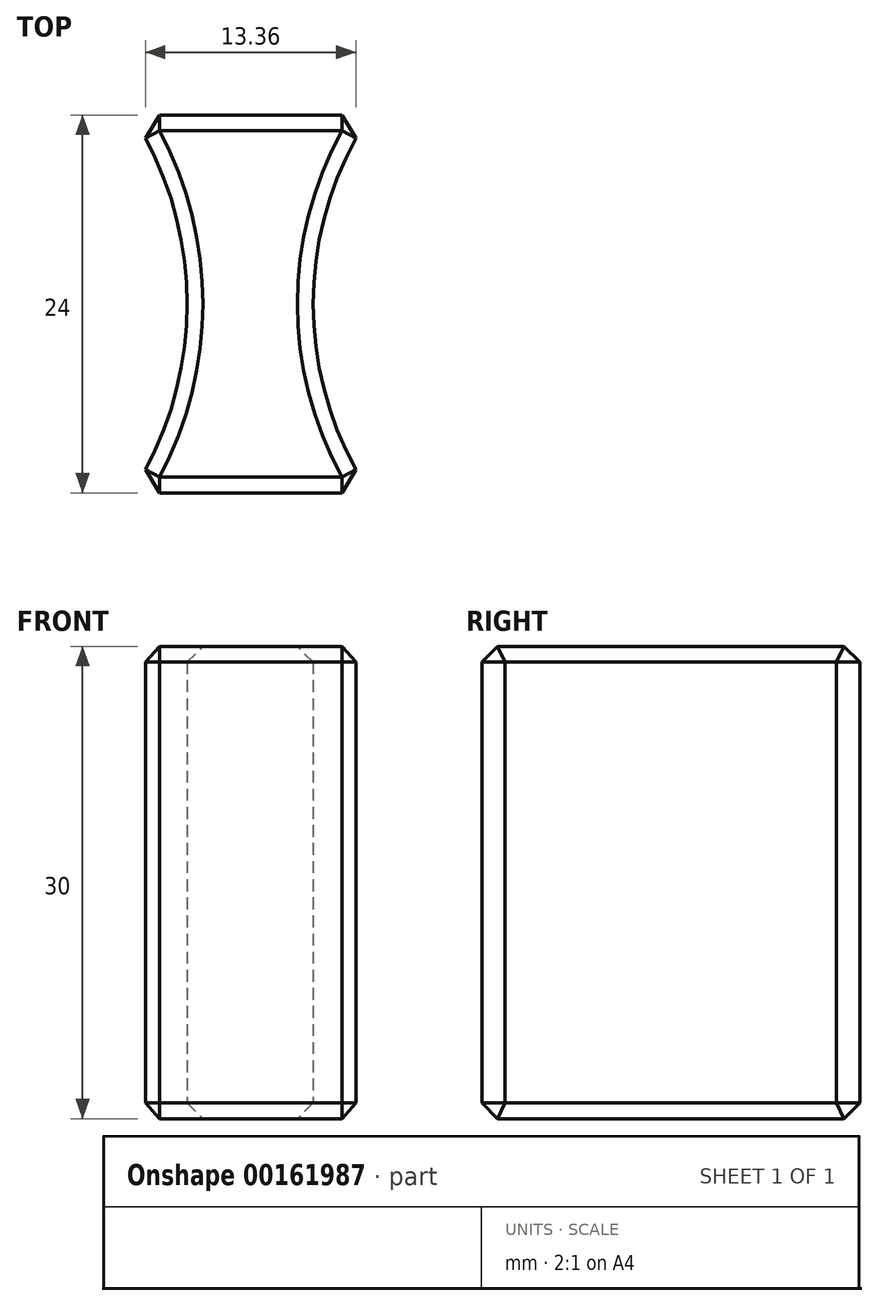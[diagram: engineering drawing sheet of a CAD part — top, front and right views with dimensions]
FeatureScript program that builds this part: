
annotation { "Feature Type Name" : "Feature", "Feature Type Description" : "" }
export const myFeature = defineFeature(function(context is Context, id is Id, definition is map)
    precondition{}
    {
        {
            var Q0;
            Q0=qCreatedBy(makeId("Top.planeOp"),FACE);
            var sketch = newSketch(context, id + "F0", { "sketchPlane" : qUnion([Q0])});
            skLineSegment(sketch, "E0", {"start": v(0, 0) * mm, "end": v(20.37, 0) * mm, "construction": true});
            skLineSegment(sketch, "E1", {"start": v(-1.7, 0) * mm, "end": v(-70.23, 0) * mm, "construction": true});
            skArc(sketch, "E2", {"start": v(-7.95, 12) * mm, "mid": v(-11.56, 0) * mm, "end": v(-7.95, -12) * mm});
            skLineSegment(sketch, "E3", {"start": v(-68.97, -12) * mm, "end": v(35.27, -12) * mm, "construction": true});
            skLineSegment(sketch, "E4", {"start": v(-67.76, 12) * mm, "end": v(33.68, 12) * mm, "construction": true});
            skLineSegment(sketch, "E5", {"start": v(-23.08, 12) * mm, "end": v(-7.95, 12) * mm});
            skLineSegment(sketch, "E6", {"start": v(-23.08, -12) * mm, "end": v(-7.95, -12) * mm});
            skArc(sketch, "E7.trimOffspring", {"start": v(-23.08, -12) * mm, "mid": v(-19.56, 0) * mm, "end": v(-23.08, 12) * mm});
            skSolve(sketch);
        }
        {
            var Q0;
            Q0=makeQuery(id+"F0.imprint","IMPRINT",FACE,{"disambiguationData":[TD([[makeQuery(id+"F0.imprint","IMPRINT",EDGE,{"derivedFrom":sQuery(id+"F0.wireOp",EDGE,"E2")}),-1.0]])]});
            extrude(context, id + "F1", {"entities" : qUnion([Q0]), "depth" : 30 * mm});
        }
        {
            var Q0;
            Q0=makeQuery(id+"F1.opExtrude","CAP_EDGE",EDGE,{"disambiguationData":[OSD([sQuery(id+"F0.wireOp",EDGE,"E2")])],"isStart":false});
            var Q1;
            Q1=makeQuery(id+"F1.opExtrude","CAP_EDGE",EDGE,{"disambiguationData":[OSD([sQuery(id+"F0.wireOp",EDGE,"E6")])],"isStart":false});
            var Q2;
            Q2=makeQuery(id+"F1.opExtrude","CAP_EDGE",EDGE,{"disambiguationData":[OSD([sQuery(id+"F0.wireOp",EDGE,"E7.trimOffspring")])],"isStart":false});
            var Q3;
            Q3=makeQuery(id+"F1.opExtrude","CAP_EDGE",EDGE,{"disambiguationData":[OSD([sQuery(id+"F0.wireOp",EDGE,"E5")])],"isStart":false});
            var Q4;
            Q4=makeQuery(id+"F1.opExtrude","CAP_EDGE",EDGE,{"disambiguationData":[OSD([sQuery(id+"F0.wireOp",EDGE,"E6")])],"isStart":true});
            var Q5;
            Q5=makeQuery(id+"F1.opExtrude","CAP_EDGE",EDGE,{"disambiguationData":[OSD([sQuery(id+"F0.wireOp",EDGE,"E2")])],"isStart":true});
            var Q6;
            Q6=makeQuery(id+"F1.opExtrude","CAP_EDGE",EDGE,{"disambiguationData":[OSD([sQuery(id+"F0.wireOp",EDGE,"E5")])],"isStart":true});
            var Q7;
            Q7=makeQuery(id+"F1.opExtrude","SWEPT_FACE",FACE,{"disambiguationData":[OSD([sQuery(id+"F0.wireOp",EDGE,"E7.trimOffspring")])]});
            var Q8;
            Q8=makeQuery(id+"F1.opExtrude","SWEPT_FACE",FACE,{"disambiguationData":[OSD([sQuery(id+"F0.wireOp",EDGE,"E2")])]});
            chamfer(context, id + "F2", {"entities" : qUnion([Q0, Q1, Q2, Q3, Q4, Q5, Q6, Q7, Q8]), "width" : 1 * mm, "tangentPropagation" : true});
        }
    });
